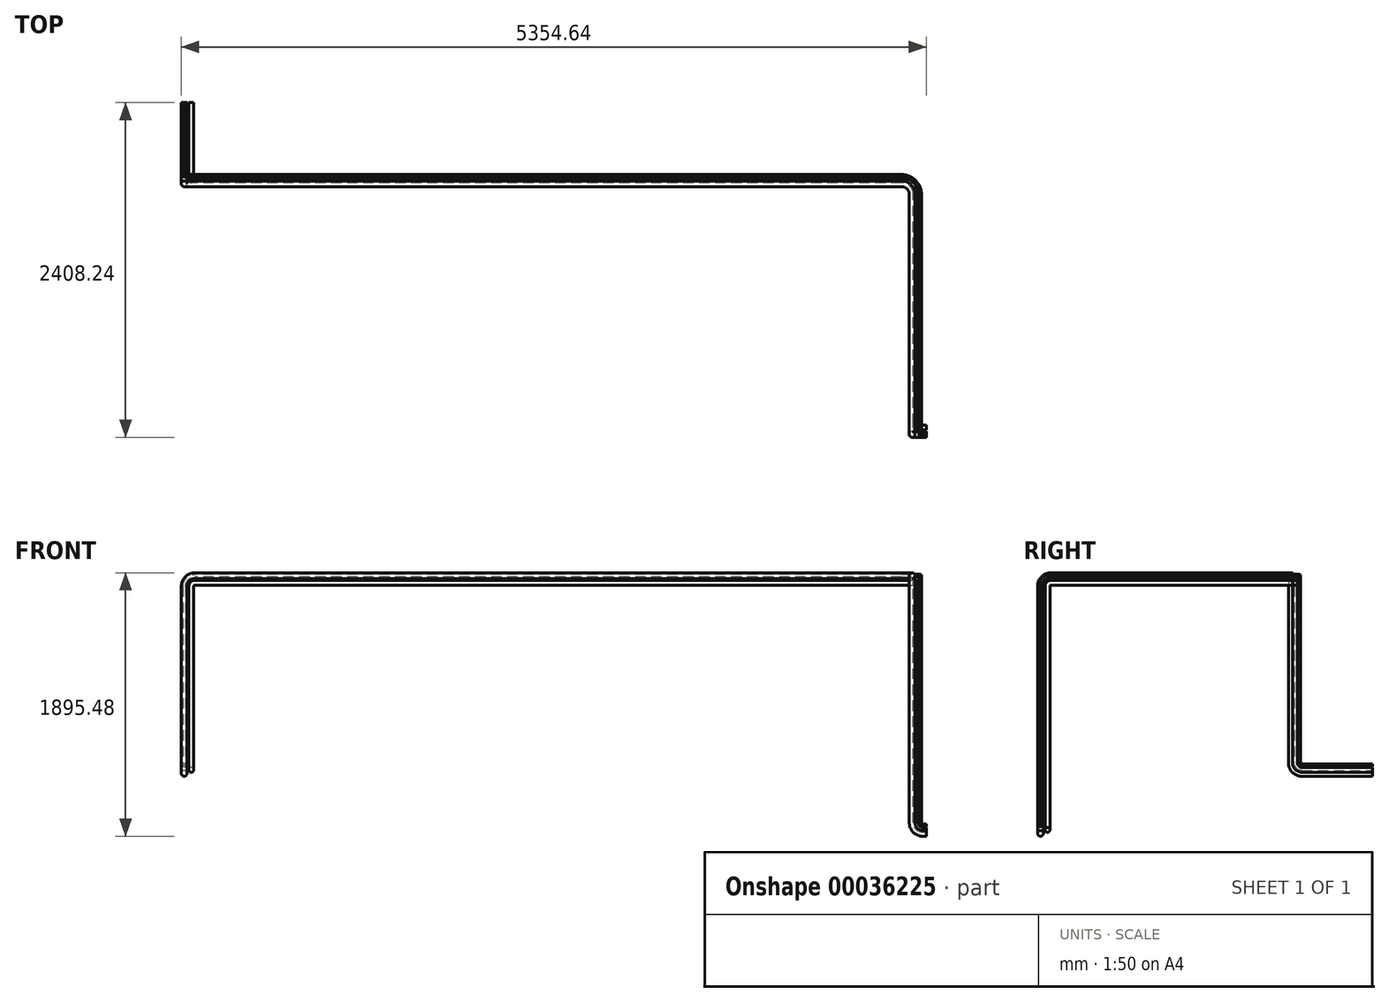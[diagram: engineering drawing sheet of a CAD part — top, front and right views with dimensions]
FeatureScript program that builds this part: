
annotation { "Feature Type Name" : "Feature", "Feature Type Description" : "" }
export const myFeature = defineFeature(function(context is Context, id is Id, definition is map)
    precondition{}
    {
        {
            var Q0;
            Q0=qCreatedBy(makeId("Right.planeOp"),FACE);
            var sketch = newSketch(context, id + "F0", { "sketchPlane" : qUnion([Q0])});
            skCircle(sketch, "E0", {"center": v(0, 0) * mm, "radius": 20.64 * mm});
            skCircle(sketch, "E1", {"center": v(0, 57.15) * mm, "radius": 9.53 * mm});
            skCircle(sketch, "E2", {"center": v(50.8, 25.4) * mm, "radius": 17.46 * mm});
            skSolve(sketch);
        }
        {
            var Q0;
            Q0=qCreatedBy(makeId("Front.planeOp"),FACE);
            var sketch = newSketch(context, id + "F1", { "sketchPlane" : qUnion([Q0])});
            skLineSegment(sketch, "E3", {"start": v(0, 0) * mm, "end": v(-25.4, 0) * mm});
            skArc(sketch, "E4", {"start": v(-101.6, 76.2) * mm, "mid": v(-79.28, 22.32) * mm, "end": v(-25.4, 0) * mm});
            skLineSegment(sketch, "E5", {"start": v(-101.6, 76.2) * mm, "end": v(-101.6, 1778) * mm});
            skSolve(sketch);
        }
        {
            var Q0;
            Q0=sQuery(id+"F1.wireOp",VERTEX,"E5.end");
            var Q1;
            Q1=qCreatedBy(makeId("Right.planeOp"),FACE);
            cPlane(context, id + "F2", {"entities" : qUnion([Q0, Q1]), "cplaneType" : CPlaneType.PLANE_POINT, "offset" : 152.4 * mm, "width" : 152.4 * mm, "height" : 152.4 * mm});
        }
        {
            var Q0;
            Q0=qCreatedBy(id+"F2.planeOp",FACE);
            var sketch = newSketch(context, id + "F3", { "sketchPlane" : qUnion([Q0])});
            skArc(sketch, "E6", {"start": v(76.2, 1854.2) * mm, "mid": v(22.32, 1831.88) * mm, "end": v(0, 1778) * mm});
            skLineSegment(sketch, "E7", {"start": v(76.2, 1854.2) * mm, "end": v(1727.2, 1854.2) * mm});
            skSolve(sketch);
        }
        {
            var Q0;
            Q0=qCreatedBy(makeId("Top.planeOp"),FACE);
            var Q1;
            Q1=sQuery(id+"F3.wireOp",VERTEX,"E7.end");
            cPlane(context, id + "F4", {"entities" : qUnion([Q0, Q1]), "cplaneType" : CPlaneType.PLANE_POINT, "offset" : 152.4 * mm, "width" : 152.4 * mm, "height" : 152.4 * mm});
        }
        {
            var Q0;
            Q0=qCreatedBy(id+"F4.planeOp",FACE);
            var sketch = newSketch(context, id + "F5", { "sketchPlane" : qUnion([Q0])});
            skArc(sketch, "E8", {"start": v(-101.6, 1727.2) * mm, "mid": v(-123.92, 1781.08) * mm, "end": v(-177.8, 1803.4) * mm});
            skLineSegment(sketch, "E9", {"start": v(-177.8, 1803.4) * mm, "end": v(-5257.8, 1803.4) * mm});
            skSolve(sketch);
        }
        {
            var Q0;
            Q0=qCreatedBy(makeId("Front.planeOp"),FACE);
            var Q1;
            Q1=sQuery(id+"F5.wireOp",VERTEX,"E9.end");
            cPlane(context, id + "F6", {"entities" : qUnion([Q0, Q1]), "cplaneType" : CPlaneType.PLANE_POINT, "offset" : 152.4 * mm, "width" : 152.4 * mm, "height" : 152.4 * mm});
        }
        {
            var Q0;
            Q0=qCreatedBy(id+"F6.planeOp",FACE);
            var sketch = newSketch(context, id + "F7", { "sketchPlane" : qUnion([Q0])});
            skLineSegment(sketch, "E10", {"start": v(-5334, 508) * mm, "end": v(-5334, 1778) * mm});
            skArc(sketch, "E11", {"start": v(-5334, 1778) * mm, "mid": v(-5311.68, 1831.88) * mm, "end": v(-5257.8, 1854.2) * mm});
            skSolve(sketch);
        }
        {
            var Q0;
            Q0=qCreatedBy(makeId("Right.planeOp"),FACE);
            var Q1;
            Q1=sQuery(id+"F7.wireOp",VERTEX,"E10.start");
            cPlane(context, id + "F8", {"entities" : qUnion([Q0, Q1]), "cplaneType" : CPlaneType.PLANE_POINT, "offset" : 152.4 * mm, "width" : 152.4 * mm, "height" : 152.4 * mm});
        }
        {
            var Q0;
            Q0=qCreatedBy(id+"F8.planeOp",FACE);
            var sketch = newSketch(context, id + "F9", { "sketchPlane" : qUnion([Q0])});
            skLineSegment(sketch, "E12", {"start": v(2387.6, 431.8) * mm, "end": v(1879.6, 431.8) * mm});
            skArc(sketch, "E13", {"start": v(1879.6, 431.8) * mm, "mid": v(1825.72, 454.12) * mm, "end": v(1803.4, 508) * mm});
            skSolve(sketch);
        }
        {
            var Q0;
            Q0 = qSketchRegion(id + "F0", true);
            var Q1;
            Q1=sQuery(id+"F1.wireOp",EDGE,"E3");
            var Q2;
            Q2=sQuery(id+"F1.wireOp",EDGE,"E4");
            var Q3;
            Q3=sQuery(id+"F1.wireOp",EDGE,"E5");
            var Q4;
            Q4=sQuery(id+"F3.wireOp",EDGE,"E6");
            var Q5;
            Q5=sQuery(id+"F3.wireOp",EDGE,"E7");
            var Q6;
            Q6=sQuery(id+"F5.wireOp",EDGE,"E8");
            var Q7;
            Q7=sQuery(id+"F5.wireOp",EDGE,"E9");
            var Q8;
            Q8=sQuery(id+"F7.wireOp",EDGE,"E11");
            var Q9;
            Q9=sQuery(id+"F7.wireOp",EDGE,"E10");
            var Q10;
            Q10=sQuery(id+"F9.wireOp",EDGE,"E13");
            var Q11;
            Q11=sQuery(id+"F9.wireOp",EDGE,"E12");
            sweep(context, id + "F10", {"profiles" : qUnion([Q0]), "path" : qUnion([Q1, Q2, Q3, Q4, Q5, Q6, Q7, Q8, Q9, Q10, Q11])});
        }
    });
